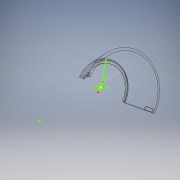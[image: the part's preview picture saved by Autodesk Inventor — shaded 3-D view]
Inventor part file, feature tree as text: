
AUTODESK INVENTOR PART (.ipt)
format: ipt  version: 2018 (Build 220112000, 112)  size: 214,016 bytes
history: native  units: mm
features: sketch x4, revolve x1, extrude x1
ambient origin geometry x8: Origin, YZ Plane, XZ Plane, XY Plane, X Axis, Y Axis, Z Axis, Center Point
bodies: Body1 (feature_tree)
feature tree (6):
  sketch  "Sketch68"  dims[d600=1.4mm d601=2.7mm]
  sketch  "Sketch184"  dims[d603=1.265mm d604=180.0deg]
  revolve  "Revolution5"  [1 undecoded]
  extrude  "Extrusion162"  TaperAngle=180.0deg  [1 undecoded]
  sketch  "Sketch213"  dims[d606=0.0mm]
  sketch  "Sketch214"  dims[d612=1.875mm d613=8.0mm d614=0.7mm d615=0.7mm d616=3.0mm d617=0.0mm d21=1.0mm d22=1.0mm]
note: 2 required parameter values undecoded (feature->parameter linkage not recoverable at this tier; creation-order binding heuristic only, values carry confidence <= 0.55)